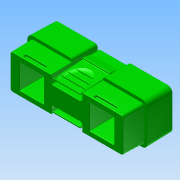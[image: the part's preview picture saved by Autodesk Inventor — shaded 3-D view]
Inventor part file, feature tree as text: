
AUTODESK INVENTOR PART (.ipt)
format: ipt  version: 2015 (Build 190159000, 159)  size: 1,796,608 bytes
history: native  units: in
note: dims shown in document units (in); Inventor stores cm internally (conversion verified against a paired STEP export)
features: extrude x8, fillet x8, sketch x7, draft x4, mirror x2, projected_geometry x1
ambient origin geometry x8: Origin, YZ Plane, XZ Plane, XY Plane, X Axis, Y Axis, Z Axis, Center Point
bodies: Solid1 (feature_tree)
feature tree (30):
  sketch  "Sketch1"  dims[d0=0.34in d1=0.8in]
  extrude  "Extrusion1"  Depth=0.8in
  extrude  "Extrusion2"  Depth=0.2975in
  extrude  "Extrusion3"  Depth=0.06in
  draft  "FaceDraft1"
  draft  "FaceDraft2"
  extrude  "Extrusion4"  Depth=0.5in TaperAngle=0.0deg
  extrude  "Extrusion5"  Depth=0.15in
  fillet  "Fillet1"  Radius=0.33in
  fillet  "Fillet2"  Radius=0.0069in
  extrude  "Extrusion6"  Depth=0.17in
  draft  "FaceDraft3"
  fillet  "Fillet3"  Radius=0.17in
  fillet  "Fillet4"  Radius=0.04in
  fillet  "Fillet5"  Radius=0.09in
  extrude  "Extrusion7"  Depth=0.03in
  extrude  "Extrusion8"  Depth=0.33in
  draft  "FaceDraft4"
  fillet  "Fillet6"  Radius=0.0206in
  fillet  "Fillet7"  Radius=0.0412in
  fillet  "Fillet8"  Radius=0.2625in
  mirror  "Mirror1"
  mirror  "Mirror2"
  sketch  "Sketch2"  dims[d2=0.175in d3=0.2975in]
  sketch  "Sketch3"  dims[d4=0.06in d5=0.06in]
  sketch  "Sketch4"  dims[d6=0.4in d7=0.0in d8=0.5in d9=0.0in]
  projected_geometry  "Projected Loop1"
  sketch  "Sketch5"  dims[d11=0.8in d12=0.15in d13=0.33in d14=0.0in d15=0.0069in]
  sketch  "Sketch6"  dims[d16=0.0069in d17=0.17in d18=0.17in d19=0.04in d20=0.09in]
  sketch  "Sketch7"  dims[d21=0.84in d22=0.03in d24=0.33in d25=0.0206in d26=0.0412in d27=0.2625in d28=0.0in d31=0.25in d32=0.1in d33=0.2in d34=0.6174in d35=0.01in d36=0.02in d37=0.0in d38=0.05in d39=0.185in d40=0.02in d41=0.125in d42=0.24in d43=0.36in d44=0.26in d45=0.01in d46=0.01in d47=0.0in d48=0.0137in d49=0.4in d50=0.06in d51=0.48in d52=0.3in d53=0.04in d54=0.0in d55=0.2375in d56=0.47in d57=0.186in d58=0.47in d59=0.0in d60=0.0069in d61=0.05in d62=0.01in d63=0.005in d64=0.1in]
